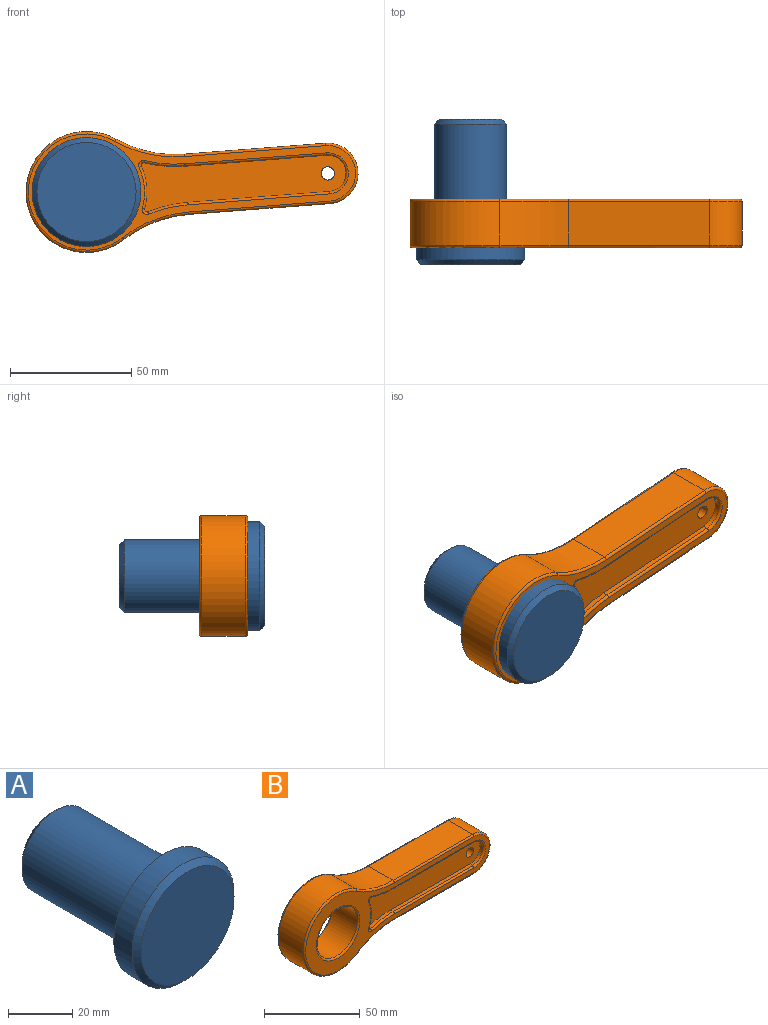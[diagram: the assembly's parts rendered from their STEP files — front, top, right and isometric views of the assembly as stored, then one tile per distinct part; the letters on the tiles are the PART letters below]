
ASSEMBLY  parts=2 mates=1
PART A: 9 faces, bbox 45x60x45 mm
  f0: cylinder r=15mm len=48mm, axis (0,-1,0), area 4523.9mm2, adj f4,f5
  f1: plane 26x26mm, normal (0,1,0), area 511.3mm2, adj f5,f8
  f2: cylinder r=22.5mm len=45mm, axis (0,1,0), area 1131mm2, adj f4,f6
  f3: plane 41x41mm, normal (0,-1,0), area 1320.3mm2, adj f6
  f4: plane 45x45mm, normal (0,1,0), area 883.6mm2, adj f0,f2
  f5: cone r=15mm half-angle=45deg, axis (0,-1,0), area 248.8mm2, adj f0,f1
  f6: cone r=20.5mm half-angle=45deg, axis (0,1,0), area 382.1mm2, adj f2,f3
  f7: cone r=0mm half-angle=59deg, axis (0,1,0), area 22.9mm2, adj f8
  f8: cylinder r=2.5mm len=15mm, axis (0,1,0), area 235.6mm2, adj f1,f7
PART B: 60 faces, bbox 140.6x20x54.1 mm
  f0: plane 58.54x18mm, normal (0,0,1), area 1053.8mm2, adj f3,f6,f27,f33
  f1: cylinder r=25mm len=50mm, axis (0,1,0), area 1940.8mm2, adj f6,f7,f23,f29
  f2: plane 58.54x18mm, normal (0,0,-1), area 1053.8mm2, adj f3,f7,f26,f32
  f3: cylinder r=12.5mm len=25mm, axis (0,1,0), area 706.9mm2, adj f0,f2,f28,f34
  f4: plane 135.5x48mm, normal (0,-1,0), area 1605.2mm2, adj f29,f30,f31,f32,f33,f34,f46,f47
  f5: cylinder r=15mm len=30mm, axis (0,-1,0), area 1696.5mm2, adj f55,f56
  f6: cylinder r=50mm len=27.64mm, axis (0,1,0), area 527.1mm2, adj f0,f1,f25,f31
  f7: cylinder r=50mm len=27.64mm, axis (0,1,0), area 527.1mm2, adj f1,f2,f24,f30
  f8: cylinder r=25mm len=17.67mm, axis (0,-1,0), area 36.1mm2, adj f14,f45,f47,f48
  f9: cylinder r=55mm len=16.83mm, axis (0,-1,0), area 34.2mm2, adj f10,f14,f48,f52
  f10: plane 58.54x2mm, normal (0,0,1), area 117.1mm2, adj f9,f11,f14,f54
  f11: cylinder r=7.5mm len=15mm, axis (0,-1,0), area 47.1mm2, adj f10,f12,f14,f53
  f12: plane 58.54x2mm, normal (0,0,-1), area 117.1mm2, adj f11,f13,f14,f51
  f13: cylinder r=55mm len=16.83mm, axis (0,-1,0), area 34.2mm2, adj f12,f14,f45,f49
  f14: plane 84.18x20.37mm, normal (0,-1,0), area 1230.4mm2, adj f8,f9,f10,f11,f12,f13,f45,f48
  f15: plane 135.5x48mm, normal (0,1,0), area 1605.2mm2, adj f23,f24,f25,f26,f27,f28,f36,f38
  f16: cylinder r=25mm len=17.67mm, axis (0,1,0), area 36.1mm2, adj f22,f35,f37,f38
  f17: cylinder r=55mm len=16.83mm, axis (0,1,0), area 34.2mm2, adj f18,f22,f37,f42
  f18: plane 58.54x2mm, normal (0,0,1), area 117.1mm2, adj f17,f19,f22,f44
  f19: cylinder r=7.5mm len=15mm, axis (0,1,0), area 47.1mm2, adj f18,f20,f22,f43
  f20: plane 58.54x2mm, normal (0,0,-1), area 117.1mm2, adj f19,f21,f22,f41
  f21: cylinder r=55mm len=16.83mm, axis (0,1,0), area 34.2mm2, adj f20,f22,f35,f39
  f22: plane 84.18x20.37mm, normal (0,1,0), area 1179.5mm2, adj f16,f17,f18,f19,f20,f21,f35,f37
  f23: torus R=24mm, axis (0,1,0), area 166.9mm2, adj f1,f15,f24,f25
  f24: torus R=51mm, axis (0,1,0), area 46.3mm2, adj f7,f15,f23,f26
  f25: torus R=51mm, axis (0,1,0), area 46.3mm2, adj f6,f15,f23,f27
  f26: cylinder r=1mm len=58.54mm, axis (-1,0,0), area 92mm2, adj f2,f15,f24,f28
  f27: cylinder r=1mm len=58.54mm, axis (1,0,0), area 92mm2, adj f0,f15,f25,f28
  f28: torus R=11.5mm, axis (0,1,0), area 59.9mm2, adj f3,f15,f26,f27
  f29: torus R=24mm, axis (0,-1,0), area 166.9mm2, adj f1,f4,f30,f31
  f30: torus R=51mm, axis (0,-1,0), area 46.3mm2, adj f4,f7,f29,f32
  f31: torus R=51mm, axis (0,-1,0), area 46.3mm2, adj f4,f6,f29,f33
  f32: cylinder r=1mm len=58.54mm, axis (-1,0,0), area 92mm2, adj f2,f4,f30,f34
  f33: cylinder r=1mm len=58.54mm, axis (1,0,0), area 92mm2, adj f0,f4,f31,f34
  f34: torus R=11.5mm, axis (0,-1,0), area 59.9mm2, adj f3,f4,f32,f33
  f35: cylinder r=1mm len=2mm, axis (0,-1,0), area 4.5mm2, adj f16,f21,f22,f36
  f36: torus R=2mm, axis (0,1,0), area 4.8mm2, adj f15,f35,f38,f39
  f37: cylinder r=1mm len=2mm, axis (0,-1,0), area 4.5mm2, adj f16,f17,f22,f40
  f38: torus R=24mm, axis (0,1,0), area 27.9mm2, adj f15,f16,f36,f40
  f39: torus R=54mm, axis (0,1,0), area 26.7mm2, adj f15,f21,f36,f41
  f40: torus R=2mm, axis (0,1,0), area 4.8mm2, adj f15,f37,f38,f42
  f41: cylinder r=1mm len=58.54mm, axis (1,0,0), area 92mm2, adj f15,f20,f39,f43
  f42: torus R=54mm, axis (0,1,0), area 26.7mm2, adj f15,f17,f40,f44
  f43: torus R=8.5mm, axis (0,1,0), area 38.8mm2, adj f15,f19,f41,f44
  f44: cylinder r=1mm len=58.54mm, axis (-1,0,0), area 92mm2, adj f15,f18,f42,f43
  f45: cylinder r=1mm len=2mm, axis (0,1,0), area 4.5mm2, adj f8,f13,f14,f46
  f46: torus R=2mm, axis (0,-1,0), area 4.8mm2, adj f4,f45,f47,f49
  f47: torus R=24mm, axis (0,-1,0), area 27.9mm2, adj f4,f8,f46,f50
  f48: cylinder r=1mm len=2mm, axis (0,1,0), area 4.5mm2, adj f8,f9,f14,f50
  f49: torus R=54mm, axis (0,-1,0), area 26.7mm2, adj f4,f13,f46,f51
  f50: torus R=2mm, axis (0,-1,0), area 4.8mm2, adj f4,f47,f48,f52
  f51: cylinder r=1mm len=58.54mm, axis (1,0,0), area 92mm2, adj f4,f12,f49,f53
  f52: torus R=54mm, axis (0,-1,0), area 26.7mm2, adj f4,f9,f50,f54
  f53: torus R=8.5mm, axis (0,-1,0), area 38.8mm2, adj f4,f11,f51,f54
  f54: cylinder r=1mm len=58.54mm, axis (-1,0,0), area 92mm2, adj f4,f10,f52,f53
  f55: torus R=16mm, axis (0,1,0), area 151.6mm2, adj f5,f15
  f56: torus R=16mm, axis (0,-1,0), area 151.6mm2, adj f4,f5
  f57: cylinder r=2.75mm len=9mm, axis (0,1,0), area 155.5mm2, adj f14,f58
  f58: plane 9.75x9.75mm, normal (0,1,0), area 50.9mm2, adj f57,f59
  f59: cylinder r=4.88mm len=9.75mm, axis (0,1,0), area 153.2mm2, adj f22,f58
PLACE A at identity fixed
PLACE B rot(axis=(0,-1,0),4.4deg) t=(0,-3,0)mm
MATE revolute B.f8 <-> A.f2  axis (0,-1,0) through (0,-10,0)mm
